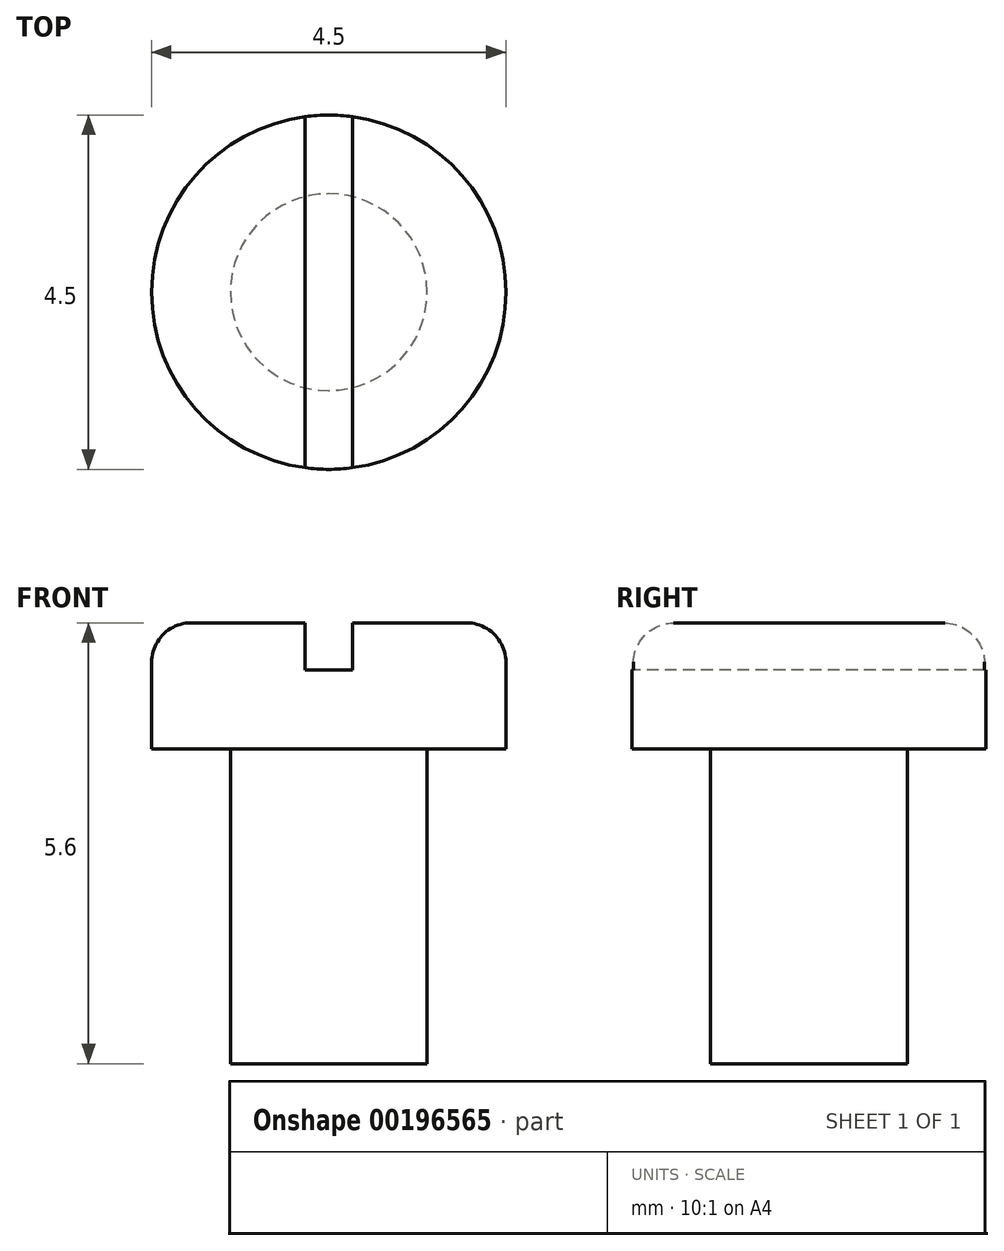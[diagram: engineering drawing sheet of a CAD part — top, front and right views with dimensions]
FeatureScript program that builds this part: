
annotation { "Feature Type Name" : "Feature", "Feature Type Description" : "" }
export const myFeature = defineFeature(function(context is Context, id is Id, definition is map)
    precondition{}
    {
        {
            var Q0;
            Q0=qCreatedBy(makeId("Front.planeOp"),FACE);
            var sketch = newSketch(context, id + "F0", { "sketchPlane" : qUnion([Q0])});
            skLineSegment(sketch, "E0", {"start": v(0, 1.6) * mm, "end": v(1.75, 1.6) * mm});
            skLineSegment(sketch, "E1", {"start": v(2.25, 1.1) * mm, "end": v(2.25, 0) * mm});
            skLineSegment(sketch, "E2", {"start": v(2.25, 0) * mm, "end": v(1.25, 0) * mm});
            skLineSegment(sketch, "E3", {"start": v(1.25, 0) * mm, "end": v(1.25, -4) * mm});
            skLineSegment(sketch, "E4", {"start": v(1.25, -4) * mm, "end": v(0, -4) * mm});
            skLineSegment(sketch, "E5", {"start": v(0, -4) * mm, "end": v(0, 1.6) * mm});
            skLineSegment(sketch, "E6", {"start": v(0, 0) * mm, "end": v(0, 3.3) * mm, "construction": true});
            skPoint(sketch, "E7.visualSharp", {"position": v(2.25, 1.6) * mm});
            skArc(sketch, "E7.filletArc", {"start": v(2.25, 1.1) * mm, "mid": v(2.1, 1.45) * mm, "end": v(1.75, 1.6) * mm});
            skSolve(sketch);
        }
        {
            var Q0;
            Q0 = qSketchRegion(id + "F0", true);
            var Q1;
            Q1=sQuery(id+"F0.wireOp",EDGE,"E6");
            revolve(context, id + "F1", {"entities" : qUnion([Q0]), "axis" : qUnion([Q1]), "revolveType" : RevolveType.FULL});
        }
        {
            var Q0;
            Q0=qCreatedBy(makeId("Front.planeOp"),FACE);
            var sketch = newSketch(context, id + "F2", { "sketchPlane" : qUnion([Q0])});
            skLineSegment(sketch, "E8.bottom", {"start": v(0.3, 1) * mm, "end": v(-0.3, 1) * mm});
            skLineSegment(sketch, "E8.top", {"start": v(0.3, 1.6) * mm, "end": v(-0.3, 1.6) * mm});
            skLineSegment(sketch, "E8.left", {"start": v(0.3, 1) * mm, "end": v(0.3, 1.6) * mm});
            skLineSegment(sketch, "E8.right", {"start": v(-0.3, 1) * mm, "end": v(-0.3, 1.6) * mm});
            skPoint(sketch, "E8.middle", {"position": v(0, 1.3) * mm});
            skSolve(sketch);
        }
        {
            var Q0;
            Q0 = qSketchRegion(id + "F2", true);
            extrude(context, id + "F3", {"entities" : qUnion([Q0]), "operationType" : NewBodyOperationType.REMOVE, "endBound" : BoundingType.THROUGH_ALL, "oppositeDirection" : true, "depth" : 25 * mm, "hasSecondDirection" : true, "secondDirectionBound" : SecondDirectionBoundingType.THROUGH_ALL, "secondDirectionOppositeDirection" : false, "secondDirectionDepth" : 25 * mm});
        }
    });
